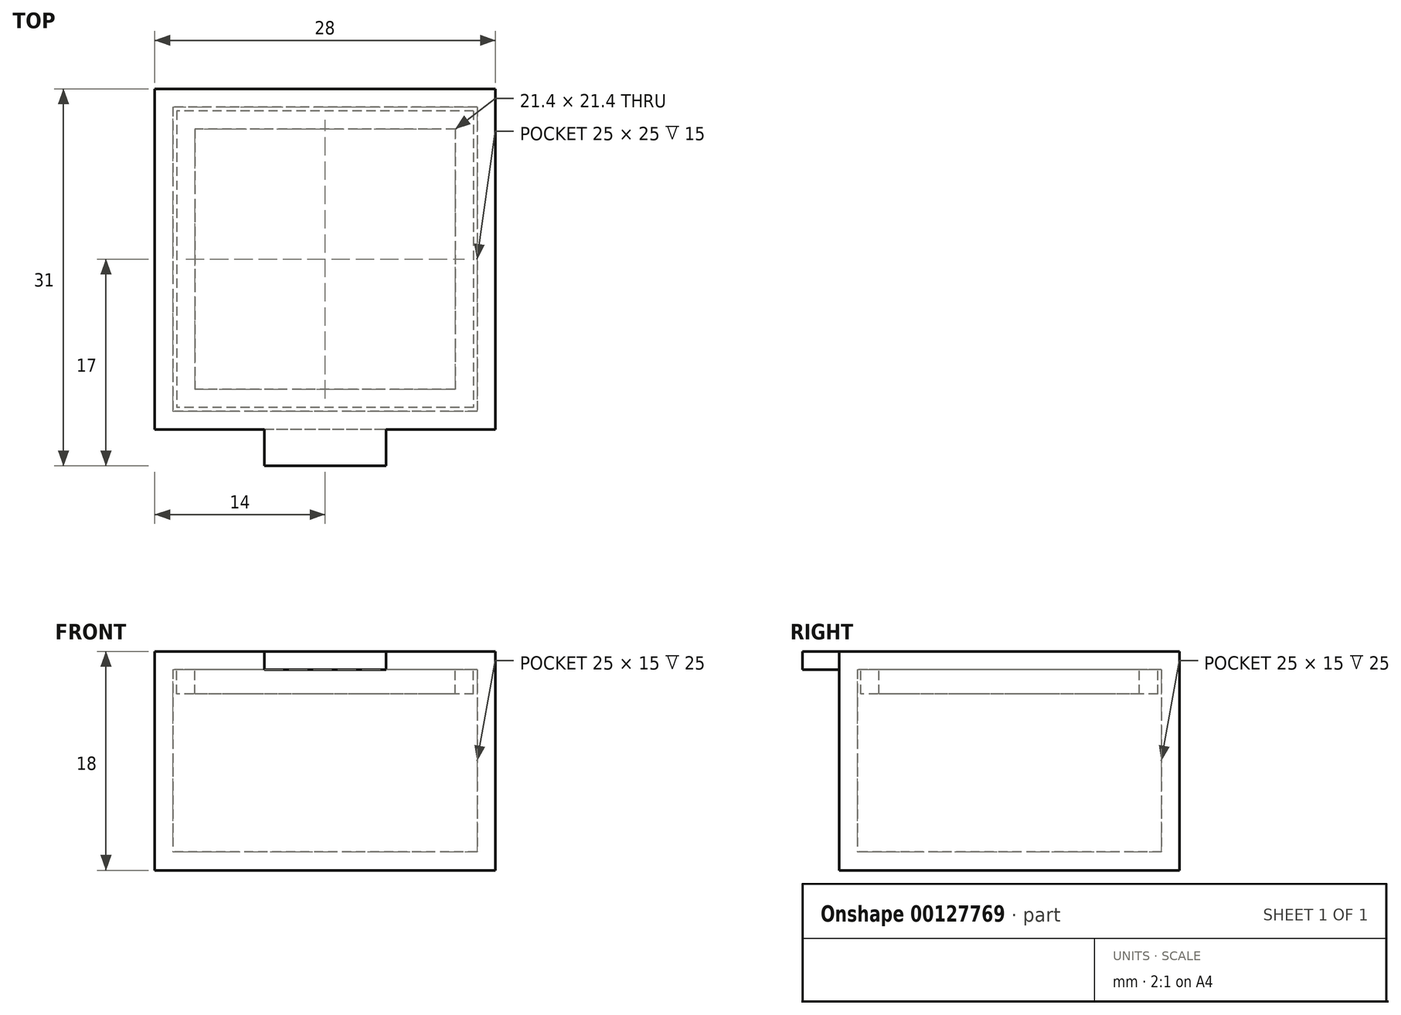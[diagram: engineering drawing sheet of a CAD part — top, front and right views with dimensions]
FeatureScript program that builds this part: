
annotation { "Feature Type Name" : "Feature", "Feature Type Description" : "" }
export const myFeature = defineFeature(function(context is Context, id is Id, definition is map)
    precondition{}
    {
        {
            var Q0;
            Q0=qCreatedBy(makeId("Top.planeOp"),FACE);
            var sketch = newSketch(context, id + "F0", { "sketchPlane" : qUnion([Q0])});
            skLineSegment(sketch, "E0.bottom", {"start": v(12.5, 12.5) * mm, "end": v(-12.5, 12.5) * mm});
            skLineSegment(sketch, "E0.top", {"start": v(12.5, -12.5) * mm, "end": v(-12.5, -12.5) * mm});
            skLineSegment(sketch, "E0.left", {"start": v(12.5, 12.5) * mm, "end": v(12.5, -12.5) * mm});
            skLineSegment(sketch, "E0.right", {"start": v(-12.5, 12.5) * mm, "end": v(-12.5, -12.5) * mm});
            skPoint(sketch, "E0.middle", {"position": v(0, 0) * mm});
            skLineSegment(sketch, "E1.0", {"start": v(14, 14) * mm, "end": v(-14, 14) * mm});
            skLineSegment(sketch, "E1.1", {"start": v(14, 14) * mm, "end": v(14, -14) * mm});
            skLineSegment(sketch, "E1.2", {"start": v(14, -14) * mm, "end": v(-14, -14) * mm});
            skLineSegment(sketch, "E1.3", {"start": v(-14, 14) * mm, "end": v(-14, -14) * mm});
            skSolve(sketch);
        }
        {
            var Q0;
            Q0=makeQuery(id+"F0.imprint","IMPRINT",FACE,{"disambiguationData":[TD([[makeQuery(id+"F0.imprint","IMPRINT",EDGE,{"derivedFrom":sQuery(id+"F0.wireOp",EDGE,"E0.bottom")}),-1.0]])]});
            var Q1;
            Q1=makeQuery(id+"F0.imprint","IMPRINT",FACE,{"disambiguationData":[TD([[makeQuery(id+"F0.imprint","IMPRINT",EDGE,{"derivedFrom":sQuery(id+"F0.wireOp",EDGE,"E0.bottom")}),1.0]])]});
            extrude(context, id + "F1", {"entities" : qUnion([Q0, Q1]), "oppositeDirection" : true, "depth" : 1.5 * mm});
        }
        {
            var Q0;
            Q0=makeQuery(id+"F0.imprint","IMPRINT",FACE,{"disambiguationData":[TD([[makeQuery(id+"F0.imprint","IMPRINT",EDGE,{"derivedFrom":sQuery(id+"F0.wireOp",EDGE,"E0.bottom")}),-1.0]])]});
            extrude(context, id + "F2", {"entities" : qUnion([Q0]), "operationType" : NewBodyOperationType.ADD, "depth" : 15 * mm});
        }
        {
            var Q0;
            Q0=makeQuery(id+"F2.opExtrude","CAP_FACE",FACE,{"disambiguationData":[OSD([sQuery(id+"F0.wireOp",EDGE,"E0.bottom"),sQuery(id+"F0.wireOp",EDGE,"E0.top"),sQuery(id+"F0.wireOp",EDGE,"E0.left"),sQuery(id+"F0.wireOp",EDGE,"E0.right"),sQuery(id+"F0.wireOp",EDGE,"E1.0"),sQuery(id+"F0.wireOp",EDGE,"E1.1"),sQuery(id+"F0.wireOp",EDGE,"E1.2"),sQuery(id+"F0.wireOp",EDGE,"E1.3")])],"isStart":false});
            var sketch = newSketch(context, id + "F3", { "sketchPlane" : qUnion([Q0])});
            skLineSegment(sketch, "E2.0", {"start": v(12.5, 12.5) * mm, "end": v(-12.5, 12.5) * mm});
            skLineSegment(sketch, "E3.0", {"start": v(-12.5, 12.5) * mm, "end": v(-12.5, -12.5) * mm});
            skLineSegment(sketch, "E4.0.0", {"start": v(14, -14) * mm, "end": v(14, 14) * mm});
            skLineSegment(sketch, "E4.0.1", {"start": v(14, 14) * mm, "end": v(-14, 14) * mm});
            skLineSegment(sketch, "E4.0.2", {"start": v(-14, 14) * mm, "end": v(-14, -14) * mm});
            skLineSegment(sketch, "E4.0.3", {"start": v(-14, -14) * mm, "end": v(14, -14) * mm});
            skLineSegment(sketch, "E5.0", {"start": v(12.5, -12.5) * mm, "end": v(-12.5, -12.5) * mm});
            skLineSegment(sketch, "E6.0", {"start": v(12.5, 12.5) * mm, "end": v(12.5, -12.5) * mm});
            skLineSegment(sketch, "E7.0", {"start": v(12.2, 12.2) * mm, "end": v(-12.2, 12.2) * mm});
            skLineSegment(sketch, "E7.1", {"start": v(12.2, 12.2) * mm, "end": v(12.2, -12.2) * mm});
            skLineSegment(sketch, "E7.2", {"start": v(12.2, -12.2) * mm, "end": v(-12.2, -12.2) * mm});
            skLineSegment(sketch, "E7.3", {"start": v(-12.2, 12.2) * mm, "end": v(-12.2, -12.2) * mm});
            skLineSegment(sketch, "E8.0", {"start": v(10.7, 10.7) * mm, "end": v(-10.7, 10.7) * mm});
            skLineSegment(sketch, "E8.1", {"start": v(10.7, 10.7) * mm, "end": v(10.7, -10.7) * mm});
            skLineSegment(sketch, "E8.2", {"start": v(10.7, -10.7) * mm, "end": v(-10.7, -10.7) * mm});
            skLineSegment(sketch, "E8.3", {"start": v(-10.7, 10.7) * mm, "end": v(-10.7, -10.7) * mm});
            skSolve(sketch);
        }
        {
            var Q0;
            Q0=makeQuery(id+"F3.imprint","IMPRINT",FACE,{"disambiguationData":[TD([[makeQuery(id+"F3.imprint","IMPRINT",EDGE,{"derivedFrom":sQuery(id+"F3.wireOp",EDGE,"E7.0")}),1.0]])]});
            extrude(context, id + "F4", {"entities" : qUnion([Q0]), "oppositeDirection" : true, "depth" : 2 * mm});
        }
        {
            var Q0;
            Q0=makeQuery(id+"F3.imprint","IMPRINT",FACE,{"disambiguationData":[TD([[makeQuery(id+"F3.imprint","IMPRINT",EDGE,{"derivedFrom":sQuery(id+"F3.wireOp",EDGE,"E2.0")}),-1.0]])]});
            var Q1;
            Q1=makeQuery(id+"F3.imprint","IMPRINT",FACE,{"disambiguationData":[TD([[makeQuery(id+"F3.imprint","IMPRINT",EDGE,{"derivedFrom":sQuery(id+"F3.wireOp",EDGE,"E2.0")}),1.0]])]});
            var Q2;
            Q2=makeQuery(id+"F3.imprint","IMPRINT",FACE,{"disambiguationData":[TD([[makeQuery(id+"F3.imprint","IMPRINT",EDGE,{"derivedFrom":sQuery(id+"F3.wireOp",EDGE,"E7.0")}),1.0]])]});
            var Q3;
            Q3=makeQuery(id+"F3.imprint","IMPRINT",FACE,{"disambiguationData":[TD([[makeQuery(id+"F3.imprint","IMPRINT",EDGE,{"derivedFrom":sQuery(id+"F3.wireOp",EDGE,"E8.0")}),1.0]])]});
            extrude(context, id + "F5", {"entities" : qUnion([Q0, Q1, Q2, Q3]), "depth" : 1.5 * mm});
        }
        {
            var Q0;
            Q0=makeQuery(id+"F5.opExtrude","SWEPT_FACE",FACE,{"disambiguationData":[OSD([sQuery(id+"F3.wireOp",EDGE,"E4.0.3")])]});
            var sketch = newSketch(context, id + "F6", { "sketchPlane" : qUnion([Q0])});
            skLineSegment(sketch, "E9.0", {"start": v(14, 16.5) * mm, "end": v(-14, 16.5) * mm});
            skLineSegment(sketch, "E10.0", {"start": v(14, 15) * mm, "end": v(-14, 15) * mm});
            skLineSegment(sketch, "E11", {"start": v(-5, 16.5) * mm, "end": v(-5, 15) * mm});
            skLineSegment(sketch, "E12", {"start": v(5, 16.5) * mm, "end": v(5, 15) * mm});
            skSolve(sketch);
        }
        {
            var Q0;
            {var subQ0=sQuery(id+"F6.wireOp",EDGE,"E11");Q0=makeQuery(id+"F6.imprint","IMPRINT",FACE,{"disambiguationData":[TD([[makeQuery(id+"F6.imprint","IMPRINT",EDGE,{"derivedFrom":subQ0}),1.0]])]});}
            extrude(context, id + "F7", {"entities" : qUnion([Q0]), "operationType" : NewBodyOperationType.ADD, "depth" : 3 * mm});
        }
    });
